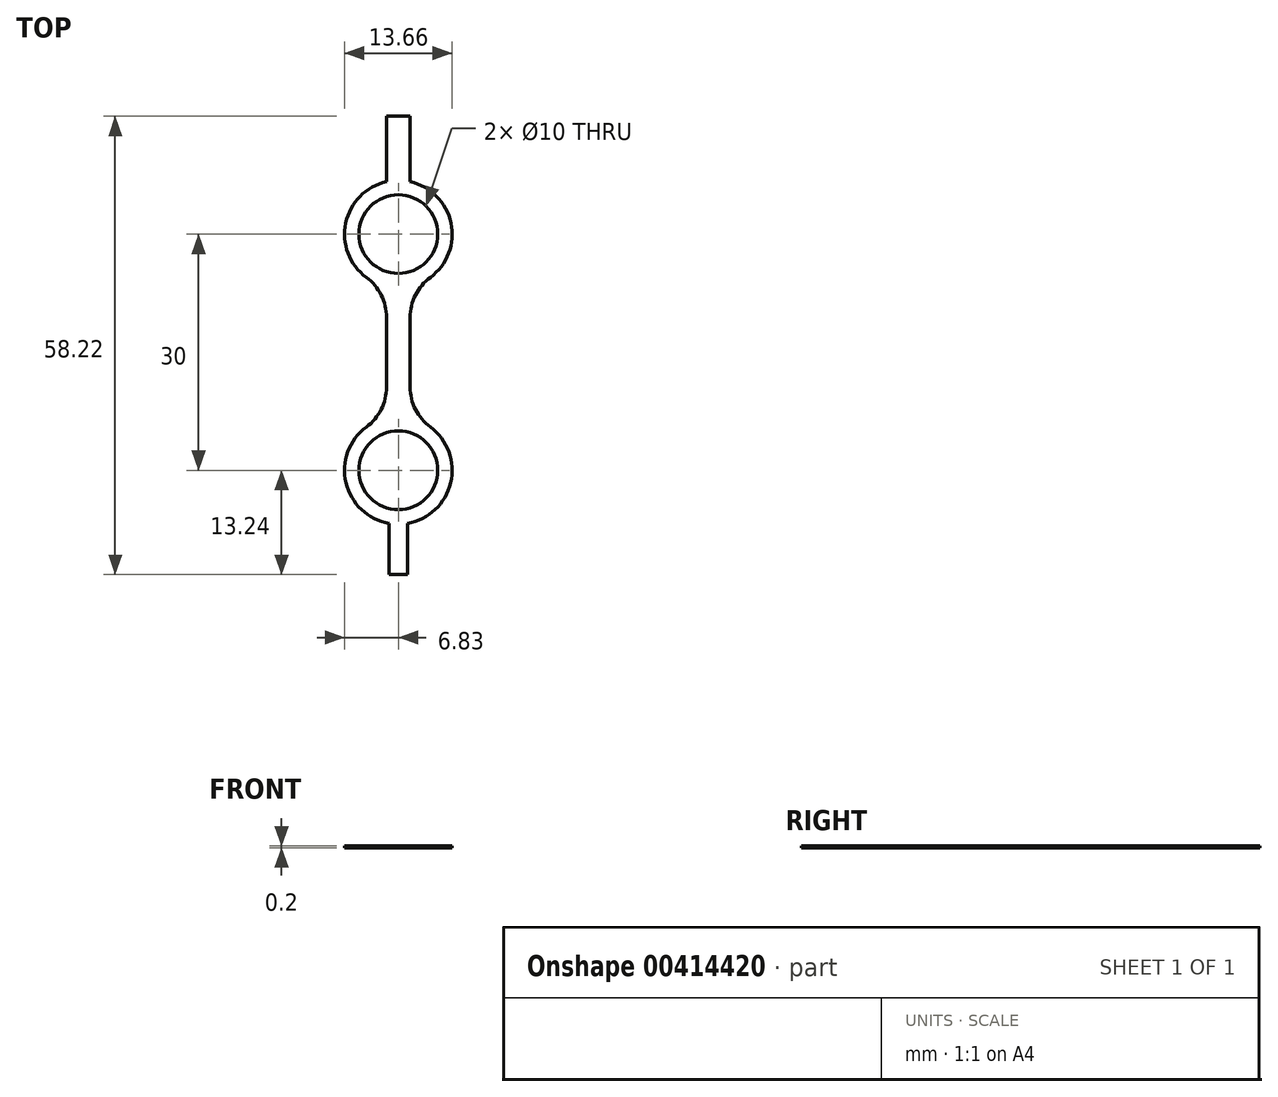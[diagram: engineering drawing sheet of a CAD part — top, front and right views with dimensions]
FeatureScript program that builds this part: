
annotation { "Feature Type Name" : "Feature", "Feature Type Description" : "" }
export const myFeature = defineFeature(function(context is Context, id is Id, definition is map)
    precondition{}
    {
        {
            var Q0;
            Q0=qCreatedBy(makeId("Top.planeOp"),FACE);
            var sketch = newSketch(context, id + "F0", { "sketchPlane" : qUnion([Q0])});
            skPoint(sketch, "E0.middle", {"position": v(0, 0) * mm});
            skCircle(sketch, "E1", {"center": v(0, 2.5) * mm, "radius": 5 * mm});
            skArc(sketch, "E2", {"start": v(-4.07, -22) * mm, "mid": v(-6.65, -29.08) * mm, "end": v(-1.16, -34.24) * mm});
            skCircle(sketch, "E3", {"center": v(0, -27.5) * mm, "radius": 5 * mm});
            skLineSegment(sketch, "E4.trimOffspring", {"start": v(-1.5, -8.1) * mm, "end": v(-1.5, -16.9) * mm});
            skLineSegment(sketch, "E5.trimOffspring", {"start": v(1.5, -8.1) * mm, "end": v(1.5, -16.9) * mm});
            skArc(sketch, "E6.filletArc", {"start": v(-4.07, -22) * mm, "mid": v(-2.18, -19.76) * mm, "end": v(-1.5, -16.9) * mm});
            skArc(sketch, "E7.filletArc", {"start": v(1.5, -16.9) * mm, "mid": v(2.18, -19.76) * mm, "end": v(4.07, -22) * mm});
            skArc(sketch, "E8.filletArc", {"start": v(4.07, -3) * mm, "mid": v(2.18, -5.24) * mm, "end": v(1.5, -8.1) * mm});
            skArc(sketch, "E9.filletArc", {"start": v(-1.5, -8.1) * mm, "mid": v(-2.18, -5.24) * mm, "end": v(-4.07, -3) * mm});
            skArc(sketch, "E10.0", {"start": v(4.07, -3) * mm, "mid": v(6.69, 3.91) * mm, "end": v(1.5, 9.17) * mm});
            skLineSegment(sketch, "E11", {"start": v(1.5, -16.9) * mm, "end": v(-1.5, -8.1) * mm, "construction": true});
            skLineSegment(sketch, "E12", {"start": v(-1.5, -16.9) * mm, "end": v(1.5, -8.1) * mm, "construction": true});
            skLineSegment(sketch, "E13.top", {"start": v(-1.5, 17.48) * mm, "end": v(1.5, 17.48) * mm});
            skLineSegment(sketch, "E13.left", {"start": v(-1.5, 9.17) * mm, "end": v(-1.5, 17.48) * mm});
            skLineSegment(sketch, "E13.right", {"start": v(1.5, 9.17) * mm, "end": v(1.5, 17.48) * mm});
            skPoint(sketch, "E13.middle", {"position": v(0, 13.32) * mm});
            skLineSegment(sketch, "E14.top", {"start": v(-1.16, -40.74) * mm, "end": v(1.16, -40.74) * mm});
            skLineSegment(sketch, "E14.left", {"start": v(-1.16, -34.24) * mm, "end": v(-1.16, -40.74) * mm});
            skLineSegment(sketch, "E14.right", {"start": v(1.16, -34.24) * mm, "end": v(1.16, -40.74) * mm});
            skPoint(sketch, "E14.middle", {"position": v(0, -37.49) * mm});
            skArc(sketch, "E15.trimOffspring", {"start": v(-1.5, 9.17) * mm, "mid": v(-6.69, 3.91) * mm, "end": v(-4.07, -3) * mm});
            skArc(sketch, "E16.trimOffspring", {"start": v(1.16, -34.24) * mm, "mid": v(6.65, -29.08) * mm, "end": v(4.07, -22) * mm});
            skSolve(sketch);
        }
        {
            var Q0;
            Q0=makeQuery(id+"F0.imprint","IMPRINT",FACE,{"disambiguationData":[TD([[makeQuery(id+"F0.imprint","IMPRINT",EDGE,{"derivedFrom":sQuery(id+"F0.wireOp",EDGE,"E1")}),-1.0]])]});
            extrude(context, id + "F1", {"entities" : qUnion([Q0]), "depth" : .2 * mm, "offsetDistance" : 25.4 * mm});
        }
    });
